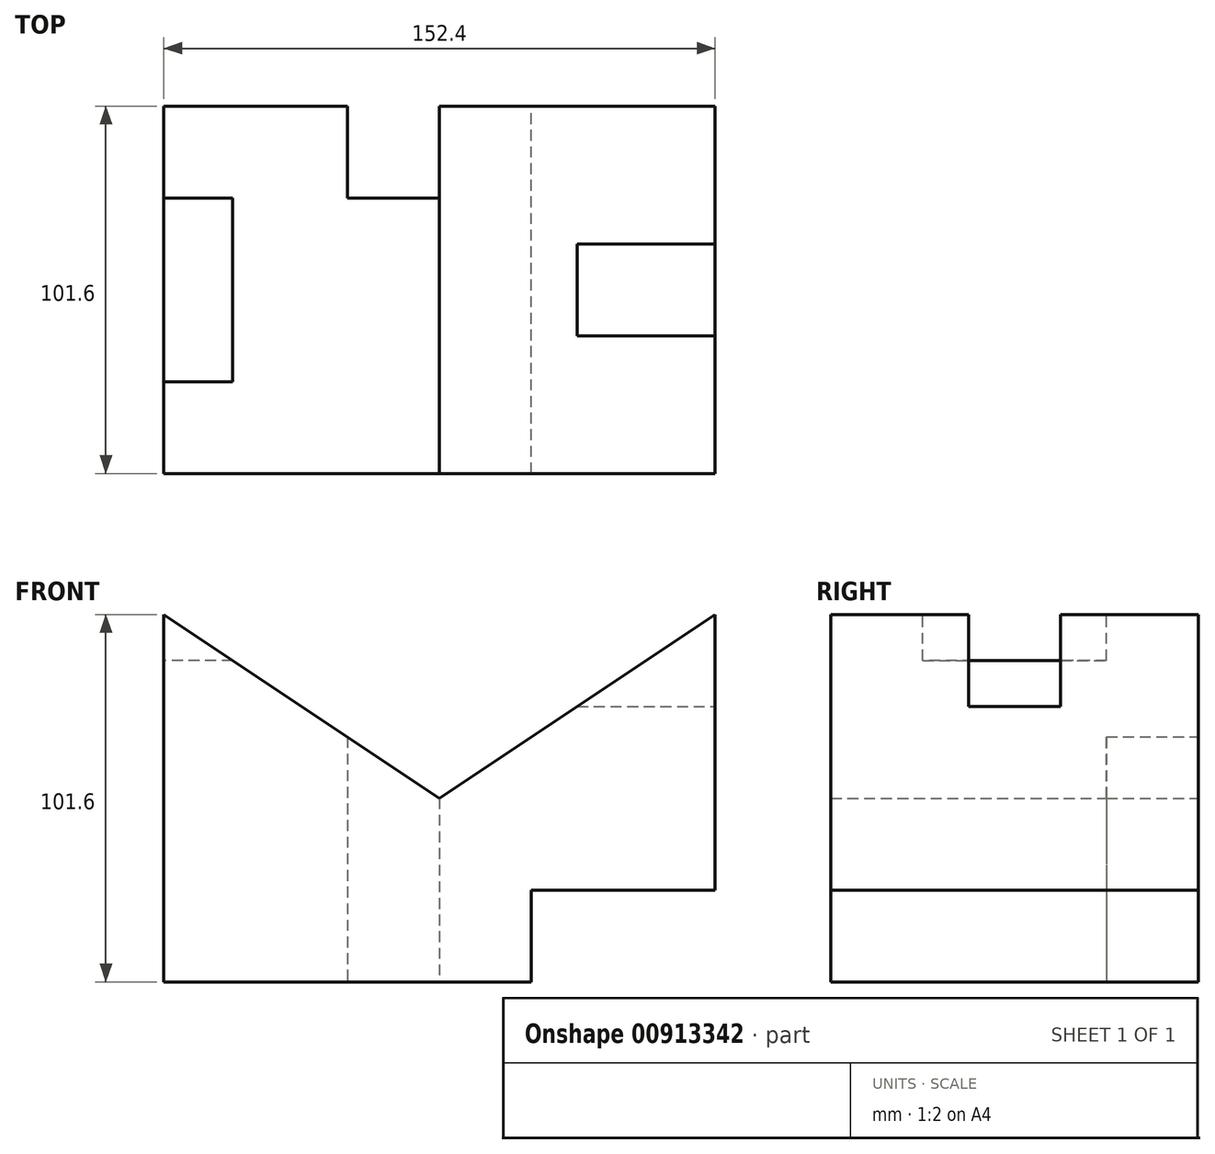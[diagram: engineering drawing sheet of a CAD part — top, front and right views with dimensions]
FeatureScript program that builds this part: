
annotation { "Feature Type Name" : "Feature", "Feature Type Description" : "" }
export const myFeature = defineFeature(function(context is Context, id is Id, definition is map)
    precondition{}
    {
        {
            var Q0;
            Q0=qCreatedBy(makeId("Front.planeOp"),FACE);
            var sketch = newSketch(context, id + "F0", { "sketchPlane" : qUnion([Q0])});
            skLineSegment(sketch, "E0.bottom", {"start": v(0, 0) * mm, "end": v(-152.4, 0) * mm});
            skLineSegment(sketch, "E0.top", {"start": v(0, 101.6) * mm, "end": v(-152.4, 101.6) * mm});
            skLineSegment(sketch, "E0.left", {"start": v(0, 0) * mm, "end": v(0, 101.6) * mm});
            skLineSegment(sketch, "E0.right", {"start": v(-152.4, 0) * mm, "end": v(-152.4, 101.6) * mm});
            skLineSegment(sketch, "E1", {"start": v(-152.4, 101.6) * mm, "end": v(0, 0) * mm});
            skLineSegment(sketch, "E2", {"start": v(0, 101.6) * mm, "end": v(-152.4, 0) * mm});
            skSolve(sketch);
        }
        {
            var Q0;
            {var subQ0=sQuery(id+"F0.wireOp",EDGE,"E0.bottom");Q0=makeQuery(id+"F0.imprint","IMPRINT",FACE,{"disambiguationData":[TD([[makeQuery(id+"F0.imprint","IMPRINT",EDGE,{"derivedFrom":subQ0}),-1.0]])]});}
            var Q1;
            {var subQ0=sQuery(id+"F0.wireOp",EDGE,"E0.left");Q1=makeQuery(id+"F0.imprint","IMPRINT",FACE,{"disambiguationData":[TD([[makeQuery(id+"F0.imprint","IMPRINT",EDGE,{"derivedFrom":subQ0}),1.0]])]});}
            var Q2;
            {var subQ0=sQuery(id+"F0.wireOp",EDGE,"E0.right");Q2=makeQuery(id+"F0.imprint","IMPRINT",FACE,{"disambiguationData":[TD([[makeQuery(id+"F0.imprint","IMPRINT",EDGE,{"derivedFrom":subQ0}),-1.0]])]});}
            extrude(context, id + "F1", {"entities" : qUnion([Q0, Q1, Q2]), "depth" : 101.6 * mm, "offsetDistance" : 25.4 * mm});
        }
        {
            var Q0;
            Q0=makeQuery(id+"F1.opExtrude","SWEPT_FACE",FACE,{"disambiguationData":[OSD([sQuery(id+"F0.wireOp",EDGE,"E0.left")])]});
            var sketch = newSketch(context, id + "F2", { "sketchPlane" : qUnion([Q0])});
            skLineSegment(sketch, "E3.bottom", {"start": v(-63.5, 101.6) * mm, "end": v(-38.1, 101.6) * mm});
            skLineSegment(sketch, "E3.top", {"start": v(-63.5, 76.2) * mm, "end": v(-38.1, 76.2) * mm});
            skLineSegment(sketch, "E3.left", {"start": v(-63.5, 101.6) * mm, "end": v(-63.5, 76.2) * mm});
            skLineSegment(sketch, "E3.right", {"start": v(-38.1, 101.6) * mm, "end": v(-38.1, 76.2) * mm});
            skLineSegment(sketch, "E4.bottom", {"start": v(-101.6, 0) * mm, "end": v(0, 0) * mm});
            skLineSegment(sketch, "E4.top", {"start": v(-101.6, 25.4) * mm, "end": v(0, 25.4) * mm});
            skLineSegment(sketch, "E4.left", {"start": v(-101.6, 0) * mm, "end": v(-101.6, 25.4) * mm});
            skLineSegment(sketch, "E4.right", {"start": v(0, 0) * mm, "end": v(0, 25.4) * mm});
            skSolve(sketch);
        }
        {
            var Q0;
            Q0 = qSketchRegion(id + "F2", true);
            extrude(context, id + "F3", {"entities" : qUnion([Q0]), "operationType" : NewBodyOperationType.REMOVE, "oppositeDirection" : true, "depth" : 50.8 * mm, "offsetDistance" : 25.4 * mm});
        }
        {
            var Q0;
            Q0=makeQuery(id+"F1.opExtrude","SWEPT_FACE",FACE,{"disambiguationData":[OSD([sQuery(id+"F0.wireOp",EDGE,"E0.bottom")])]});
            var sketch = newSketch(context, id + "F4", { "sketchPlane" : qUnion([Q0])});
            skLineSegment(sketch, "E5.bottom", {"start": v(-101.6, 0) * mm, "end": v(-76.2, 0) * mm});
            skLineSegment(sketch, "E5.top", {"start": v(-101.6, 25.4) * mm, "end": v(-76.2, 25.4) * mm});
            skLineSegment(sketch, "E5.left", {"start": v(-101.6, 0) * mm, "end": v(-101.6, 25.4) * mm});
            skLineSegment(sketch, "E5.right", {"start": v(-76.2, 0) * mm, "end": v(-76.2, 25.4) * mm});
            skSolve(sketch);
        }
        {
            var Q0;
            Q0 = qSketchRegion(id + "F4", true);
            extrude(context, id + "F5", {"entities" : qUnion([Q0]), "operationType" : NewBodyOperationType.REMOVE, "endBound" : BoundingType.THROUGH_ALL, "oppositeDirection" : true, "depth" : 25.4 * mm, "offsetDistance" : 25.4 * mm});
        }
        {
            var Q0;
            Q0=makeQuery(id+"F1.opExtrude","SWEPT_FACE",FACE,{"disambiguationData":[OSD([sQuery(id+"F0.wireOp",EDGE,"E0.right")])]});
            var sketch = newSketch(context, id + "F6", { "sketchPlane" : qUnion([Q0])});
            skLineSegment(sketch, "E6.bottom", {"start": v(25.4, 101.6) * mm, "end": v(76.2, 101.6) * mm});
            skLineSegment(sketch, "E6.top", {"start": v(25.4, 88.9) * mm, "end": v(76.2, 88.9) * mm});
            skLineSegment(sketch, "E6.left", {"start": v(25.4, 101.6) * mm, "end": v(25.4, 88.9) * mm});
            skLineSegment(sketch, "E6.right", {"start": v(76.2, 101.6) * mm, "end": v(76.2, 88.9) * mm});
            skSolve(sketch);
        }
        {
            var Q0;
            Q0 = qSketchRegion(id + "F6", true);
            extrude(context, id + "F7", {"entities" : qUnion([Q0]), "operationType" : NewBodyOperationType.REMOVE, "oppositeDirection" : true, "depth" : 25.4 * mm, "offsetDistance" : 25.4 * mm});
        }
    });
